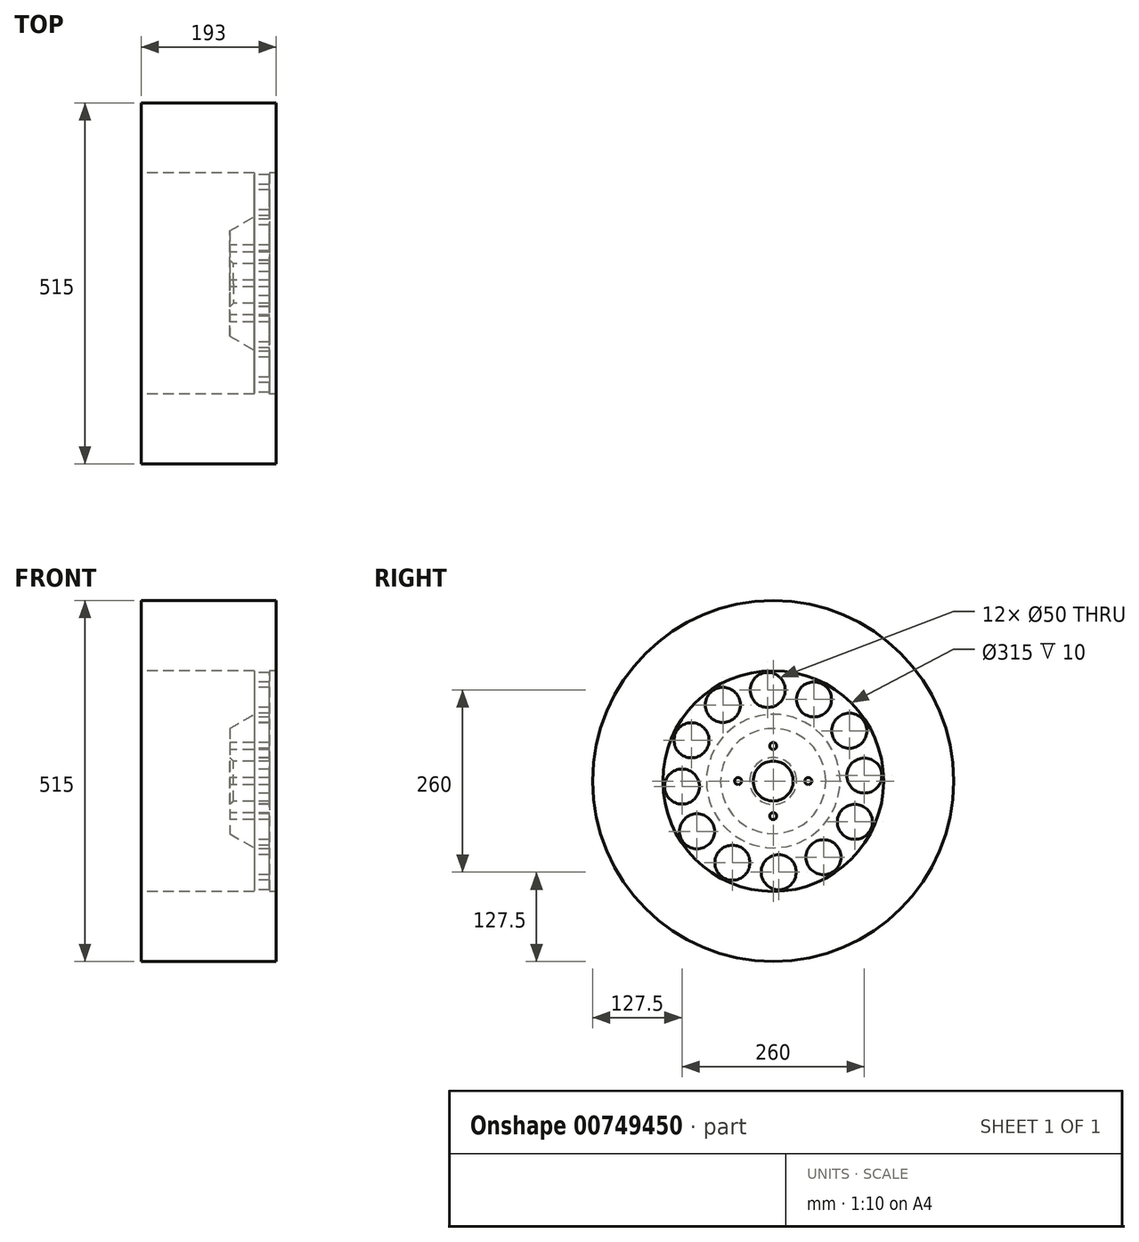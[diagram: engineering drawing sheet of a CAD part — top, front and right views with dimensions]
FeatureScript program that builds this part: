
annotation { "Feature Type Name" : "Feature", "Feature Type Description" : "" }
export const myFeature = defineFeature(function(context is Context, id is Id, definition is map)
    precondition{}
    {
        {
            var Q0;
            Q0=qCreatedBy(makeId("Front.planeOp"),FACE);
            var sketch = newSketch(context, id + "F0", { "sketchPlane" : qUnion([Q0])});
            skLineSegment(sketch, "E0", {"start": v(0, 0) * mm, "end": v(96.5, 0) * mm, "construction": true});
            skLineSegment(sketch, "E1.left", {"start": v(193, 257.5) * mm, "end": v(193, 157.5) * mm});
            skLineSegment(sketch, "E1.right", {"start": v(0, 257.5) * mm, "end": v(0, 157.5) * mm});
            skLineSegment(sketch, "E2", {"start": v(0, 257.5) * mm, "end": v(193, 257.5) * mm});
            skLineSegment(sketch, "E3", {"start": v(193, 157.5) * mm, "end": v(183, 157.5) * mm});
            skLineSegment(sketch, "E4", {"start": v(96.5, 257.5) * mm, "end": v(96.5, 0) * mm, "construction": true});
            skPoint(sketch, "E4.endSnap0", {"position": v(96.5, 157.5) * mm});
            skLineSegment(sketch, "E5", {"start": v(161.5, 157.5) * mm, "end": v(161.5, 95.2) * mm});
            skLineSegment(sketch, "E6", {"start": v(161.5, 95.2) * mm, "end": v(126.5, 75) * mm});
            skLineSegment(sketch, "E7", {"start": v(126.5, 75) * mm, "end": v(126.5, 28.5) * mm});
            skLineSegment(sketch, "E8", {"start": v(183, 157.5) * mm, "end": v(183, 28.5) * mm});
            skLineSegment(sketch, "E9.trimOffspring", {"start": v(161.5, 157.5) * mm, "end": v(0, 157.5) * mm});
            skLineSegment(sketch, "E10", {"start": v(126.5, 28.5) * mm, "end": v(183, 28.5) * mm});
            skPoint(sketch, "E11.orphan", {"position": v(183, 0) * mm});
            skPoint(sketch, "E12.orphan", {"position": v(126.5, 0) * mm});
            skSolve(sketch);
        }
        {
            var Q0;
            Q0 = qSketchRegion(id + "F0", true);
            var Q1;
            Q1=sQuery(id+"F0.wireOp",EDGE,"E0");
            revolve(context, id + "F1", {"surfaceOperationType" : NewSurfaceOperationType.NEW, "entities" : qUnion([Q0]), "axis" : qUnion([Q1]), "revolveType" : RevolveType.FULL});
        }
        {
            var Q0;
            Q0=makeQuery(id+"F1.opRevolve","SWEPT_FACE",FACE,{"disambiguationData":[OSD([sQuery(id+"F0.wireOp",EDGE,"E5")])]});
            var sketch = newSketch(context, id + "F2", { "sketchPlane" : qUnion([Q0])});
            skCircle(sketch, "E13", {"center": v(7.85, 130) * mm, "radius": 25 * mm});
            skCircle(sketch, "E14.1.0", {"center": v(-58.2, 116.5) * mm, "radius": 25 * mm});
            skCircle(sketch, "E14.2.0", {"center": v(-108.66, 71.8) * mm, "radius": 25 * mm});
            skCircle(sketch, "E14.3.0", {"center": v(-130, 7.85) * mm, "radius": 25 * mm});
            skCircle(sketch, "E14.4.0", {"center": v(-116.5, -58.2) * mm, "radius": 25 * mm});
            skCircle(sketch, "E14.5.0", {"center": v(-71.8, -108.66) * mm, "radius": 25 * mm});
            skCircle(sketch, "E14.6.0", {"center": v(-7.85, -130) * mm, "radius": 25 * mm});
            skCircle(sketch, "E14.7.0", {"center": v(58.2, -116.5) * mm, "radius": 25 * mm});
            skCircle(sketch, "E14.8.0", {"center": v(108.66, -71.8) * mm, "radius": 25 * mm});
            skCircle(sketch, "E14.9.0", {"center": v(130, -7.85) * mm, "radius": 25 * mm});
            skCircle(sketch, "E14.10.0", {"center": v(116.5, 58.2) * mm, "radius": 25 * mm});
            skCircle(sketch, "E14.11.0", {"center": v(71.8, 108.66) * mm, "radius": 25 * mm});
            skPoint(sketch, "E14.center", {"position": v(0, 0) * mm});
            skSolve(sketch);
        }
        {
            var Q0;
            Q0 = qSketchRegion(id + "F2", true);
            extrude(context, id + "F3", {"entities" : qUnion([Q0]), "operationType" : NewBodyOperationType.REMOVE, "oppositeDirection" : true, "depth" : 25 * mm, "offsetDistance" : 25 * mm});
        }
        {
            var Q0;
            Q0=makeQuery(id+"F1.opRevolve","SWEPT_FACE",FACE,{"disambiguationData":[OSD([sQuery(id+"F0.wireOp",EDGE,"E7")])]});
            var sketch = newSketch(context, id + "F4", { "sketchPlane" : qUnion([Q0])});
            skCircle(sketch, "E15", {"center": v(0, 50) * mm, "radius": 5 * mm});
            skCircle(sketch, "E16.1.0", {"center": v(-50, 0) * mm, "radius": 5 * mm});
            skCircle(sketch, "E16.2.0", {"center": v(0, -50) * mm, "radius": 5 * mm});
            skCircle(sketch, "E16.3.0", {"center": v(50, 0) * mm, "radius": 5 * mm});
            skPoint(sketch, "E16.center", {"position": v(0, 0) * mm});
            skSolve(sketch);
        }
        {
            var Q0;
            Q0=makeQuery(id+"F4.imprint","IMPRINT",FACE,{"disambiguationData":[TD([[makeQuery(id+"F4.imprint","IMPRINT",EDGE,{"derivedFrom":sQuery(id+"F4.wireOp",EDGE,"E15")}),1.0]])]});
            var Q1;
            Q1=makeQuery(id+"F4.imprint","IMPRINT",FACE,{"disambiguationData":[TD([[makeQuery(id+"F4.imprint","IMPRINT",EDGE,{"derivedFrom":sQuery(id+"F4.wireOp",EDGE,"E16.1.0")}),1.0]])]});
            var Q2;
            Q2=makeQuery(id+"F4.imprint","IMPRINT",FACE,{"disambiguationData":[TD([[makeQuery(id+"F4.imprint","IMPRINT",EDGE,{"derivedFrom":sQuery(id+"F4.wireOp",EDGE,"E16.2.0")}),1.0]])]});
            var Q3;
            Q3=makeQuery(id+"F4.imprint","IMPRINT",FACE,{"disambiguationData":[TD([[makeQuery(id+"F4.imprint","IMPRINT",EDGE,{"derivedFrom":sQuery(id+"F4.wireOp",EDGE,"E16.3.0")}),1.0]])]});
            var Q4;
            Q4=sQuery(id+"F4.wireOp",EDGE,"E15");
            var Q5;
            Q5=sQuery(id+"F4.wireOp",EDGE,"E16.1.0");
            var Q6;
            Q6=sQuery(id+"F4.wireOp",EDGE,"E16.3.0");
            var Q7;
            Q7=sQuery(id+"F4.wireOp",EDGE,"E16.2.0");
            extrude(context, id + "F5", {"entities" : qUnion([Q0, Q1, Q2, Q3]), "operationType" : NewBodyOperationType.REMOVE, "surfaceEntities" : qUnion([Q4, Q5, Q6, Q7]), "endBound" : BoundingType.THROUGH_ALL, "oppositeDirection" : true, "depth" : 25 * mm, "offsetDistance" : 25 * mm});
        }
        {
            var Q0;
            Q0=makeQuery(id+"F1.opRevolve","SWEPT_EDGE",EDGE,{"disambiguationData":[OSD([sQuery(id+"F0.wireOp",EDGE,"E7"),sQuery(id+"F0.wireOp",EDGE,"E10")])]});
            chamfer(context, id + "F6", {"entities" : qUnion([Q0]), "width" : 5 * mm, "tangentPropagation" : true});
        }
    });
